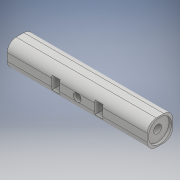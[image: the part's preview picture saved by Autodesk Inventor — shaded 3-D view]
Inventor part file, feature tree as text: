
AUTODESK INVENTOR PART (.ipt)
format: ipt  version: 2019 (Build 230136000, 136)  size: 174,080 bytes
history: native  units: mm
features: extrude x5, sketch x5, other x1, fillet x1
ambient origin geometry x8: Origin, YZ Plane, XZ Plane, XY Plane, X Axis, Y Axis, Z Axis, Center Point
bodies: Body1 (feature_tree)
feature tree (12):
  other  "Sólido1"
  extrude  "Extrusión1"  Depth=10.0mm TaperAngle=0.0deg
  sketch  "Boceto3"  dims[d4=6.3mm d6=110.0mm]
  extrude  "Extrusión2"  Depth=110.0mm
  extrude  "Extrusión3"  Depth=10.0mm
  extrude  "Extrusión4"  Depth=20.0mm
  extrude  "Extrusión5"  Depth=7.0mm
  fillet  "Empalme1"  Radius=35.0mm
  sketch  "Boceto1"  dims[d0=20.0mm d1=0.0mm d2=10.0mm d3=0.0mm]
  sketch  "Boceto5"  dims[d8=18.2mm d10=10.0mm]
  sketch  "Boceto6"  dims[d12=5.0mm d13=20.0mm]
  sketch  "Boceto7"  dims[d16=6.2mm d18=8.0mm d19=35.0mm d20=2.0mm d21=0.0mm d22=2.0mm d23=0.0mm d24=2.0mm d25=0.0mm d26=7.0mm d27=6.1mm d28=10.2mm]
